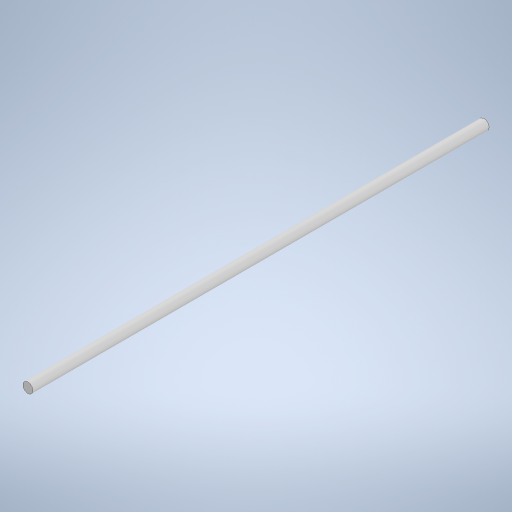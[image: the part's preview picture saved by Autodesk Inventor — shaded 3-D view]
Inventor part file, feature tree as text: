
AUTODESK INVENTOR PART (.ipt)
format: ipt  version: 2024 (Build 280153000, 153)  size: 234,496 bytes
history: native  units: mm
features: extrude x1, sketch x1
ambient origin geometry x8: Origin, YZ Plane, XZ Plane, XY Plane, X Axis, Y Axis, Z Axis, Center Point
bodies: Solid1 (feature_tree)
feature tree (2):
  extrude  "Extrusion1"  Depth=90.0mm TaperAngle=0.0deg
  sketch  "Sketch1"  dims[d0=2.0mm d1=90.0mm d2=0.0mm]
